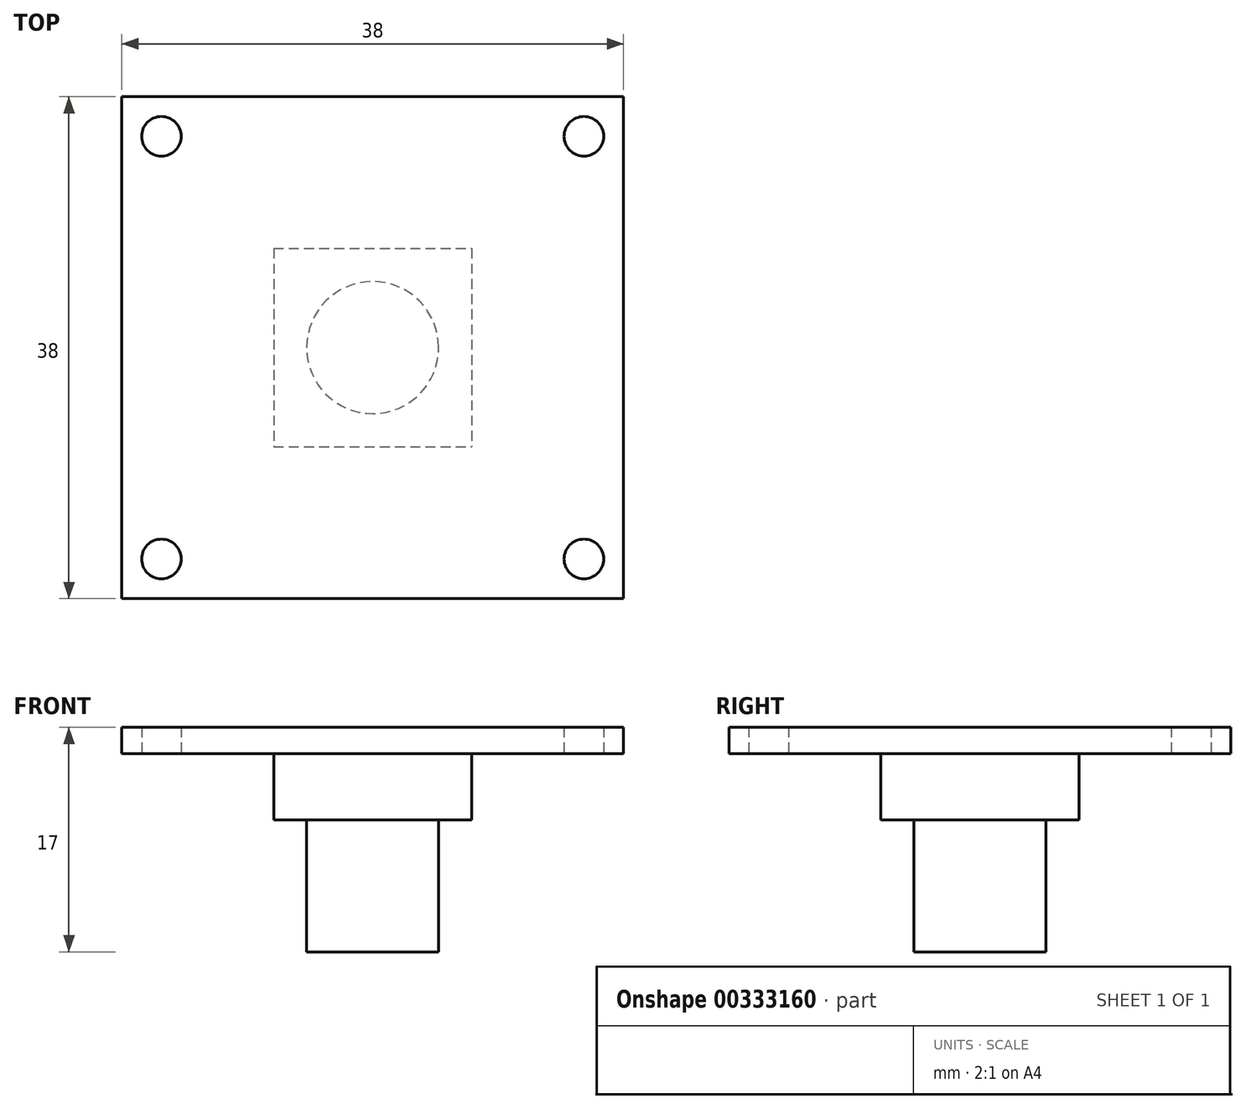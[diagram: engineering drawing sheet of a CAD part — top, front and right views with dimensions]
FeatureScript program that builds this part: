
annotation { "Feature Type Name" : "Feature", "Feature Type Description" : "" }
export const myFeature = defineFeature(function(context is Context, id is Id, definition is map)
    precondition{}
    {
        {
            var Q0;
            Q0=qCreatedBy(makeId("Top.planeOp"),FACE);
            var sketch = newSketch(context, id + "F0", { "sketchPlane" : qUnion([Q0])});
            skLineSegment(sketch, "E0.bottom", {"start": v(19, -19) * mm, "end": v(-19, -19) * mm});
            skLineSegment(sketch, "E0.top", {"start": v(19, 19) * mm, "end": v(-19, 19) * mm});
            skLineSegment(sketch, "E0.left", {"start": v(19, -19) * mm, "end": v(19, 19) * mm});
            skLineSegment(sketch, "E0.right", {"start": v(-19, -19) * mm, "end": v(-19, 19) * mm});
            skPoint(sketch, "E0.middle", {"position": v(0, 0) * mm});
            skLineSegment(sketch, "E1.bottom", {"start": v(16, -16) * mm, "end": v(-16, -16) * mm, "construction": true});
            skLineSegment(sketch, "E1.top", {"start": v(16, 16) * mm, "end": v(-16, 16) * mm, "construction": true});
            skLineSegment(sketch, "E1.left", {"start": v(16, -16) * mm, "end": v(16, 16) * mm, "construction": true});
            skLineSegment(sketch, "E1.right", {"start": v(-16, -16) * mm, "end": v(-16, 16) * mm, "construction": true});
            skCircle(sketch, "E2", {"center": v(-16, 16) * mm, "radius": 1.5 * mm});
            skCircle(sketch, "E3.1.0", {"center": v(16, 16) * mm, "radius": 1.5 * mm});
            skCircle(sketch, "E3.2.0", {"center": v(16, -16) * mm, "radius": 1.5 * mm});
            skCircle(sketch, "E3.3.0", {"center": v(-16, -16) * mm, "radius": 1.5 * mm});
            skLineSegment(sketch, "E3.anchor1", {"start": v(0, 0) * mm, "end": v(-16, 16) * mm, "construction": true});
            skLineSegment(sketch, "E3.anchor2", {"start": v(0, 0) * mm, "end": v(-16, -16) * mm, "construction": true});
            skSolve(sketch);
        }
        {
            var Q0;
            Q0=makeQuery(id+"F0.imprint","IMPRINT",FACE,{"disambiguationData":[TD([[makeQuery(id+"F0.imprint","IMPRINT",EDGE,{"derivedFrom":sQuery(id+"F0.wireOp",EDGE,"E0.bottom")}),-1.0]])]});
            extrude(context, id + "F1", {"entities" : qUnion([Q0]), "depth" : 2 * mm});
        }
        {
            var Q0;
            Q0=makeQuery(id+"F1.opExtrude","CAP_FACE",FACE,{"disambiguationData":[OSD([sQuery(id+"F0.wireOp",EDGE,"E0.bottom"),sQuery(id+"F0.wireOp",EDGE,"E0.top"),sQuery(id+"F0.wireOp",EDGE,"E0.left"),sQuery(id+"F0.wireOp",EDGE,"E0.right"),sQuery(id+"F0.wireOp",EDGE,"E2"),sQuery(id+"F0.wireOp",EDGE,"E3.1.0"),sQuery(id+"F0.wireOp",EDGE,"E3.2.0"),sQuery(id+"F0.wireOp",EDGE,"E3.3.0")])],"isStart":true});
            var sketch = newSketch(context, id + "F2", { "sketchPlane" : qUnion([Q0])});
            skLineSegment(sketch, "E4.bottom", {"start": v(-7.5, -7.5) * mm, "end": v(7.5, -7.5) * mm});
            skLineSegment(sketch, "E4.top", {"start": v(-7.5, 7.5) * mm, "end": v(7.5, 7.5) * mm});
            skLineSegment(sketch, "E4.left", {"start": v(-7.5, -7.5) * mm, "end": v(-7.5, 7.5) * mm});
            skLineSegment(sketch, "E4.right", {"start": v(7.5, -7.5) * mm, "end": v(7.5, 7.5) * mm});
            skPoint(sketch, "E4.middle", {"position": v(0, 0) * mm});
            skCircle(sketch, "E5", {"center": v(0, 0) * mm, "radius": 5 * mm});
            skSolve(sketch);
        }
        {
            var Q0;
            Q0=qSketchRegion(id+"F2",true);
            extrude(context, id + "F3", {"entities" : qUnion([Q0]), "operationType" : NewBodyOperationType.ADD, "depth" : 5 * mm});
        }
        {
            var Q0;
            Q0=makeQuery(id+"F3.boolean.opBoolean","SPLIT",FACE,{"disambiguationData":[TD([makeQuery(id+"F3.opExtrude","SWEPT_FACE",FACE,{"disambiguationData":[OSD([sQuery(id+"F2.wireOp",EDGE,"E5")])]})])],"derivedFrom":makeQuery(id+"F1.opExtrude","CAP_FACE",FACE,{"disambiguationData":[OSD([sQuery(id+"F0.wireOp",EDGE,"E0.bottom"),sQuery(id+"F0.wireOp",EDGE,"E0.top"),sQuery(id+"F0.wireOp",EDGE,"E0.left"),sQuery(id+"F0.wireOp",EDGE,"E0.right"),sQuery(id+"F0.wireOp",EDGE,"E2"),sQuery(id+"F0.wireOp",EDGE,"E3.1.0"),sQuery(id+"F0.wireOp",EDGE,"E3.2.0"),sQuery(id+"F0.wireOp",EDGE,"E3.3.0")])],"isStart":true})});
            extrude(context, id + "F4", {"entities" : qUnion([Q0]), "operationType" : NewBodyOperationType.ADD, "depth" : 15 * mm});
        }
    });
